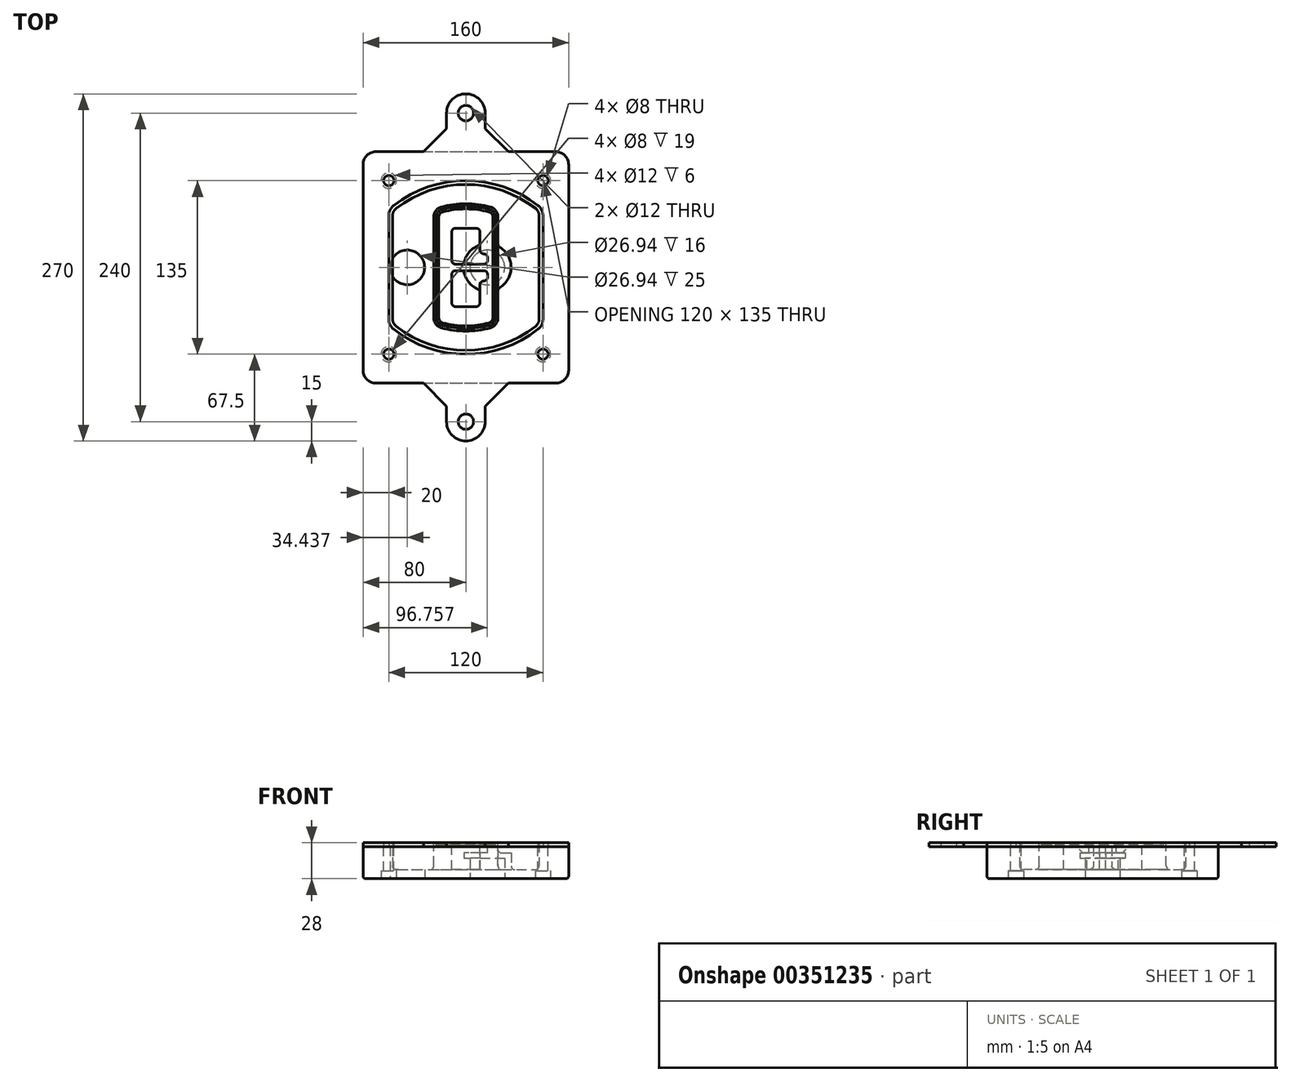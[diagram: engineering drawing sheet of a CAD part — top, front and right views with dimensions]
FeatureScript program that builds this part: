
annotation { "Feature Type Name" : "Feature", "Feature Type Description" : "" }
export const myFeature = defineFeature(function(context is Context, id is Id, definition is map)
    precondition{}
    {
        {
            var Q0;
            Q0=qCreatedBy(makeId("Top.planeOp"),FACE);
            var sketch = newSketch(context, id + "F0", { "sketchPlane" : qUnion([Q0])});
            skPoint(sketch, "E0.rect.middle", {"position": v(0, 0) * mm});
            skLineSegment(sketch, "E1.bottom", {"start": v(-70, -90) * mm, "end": v(70, -90) * mm});
            skLineSegment(sketch, "E1.top", {"start": v(-70, 90) * mm, "end": v(70, 90) * mm});
            skLineSegment(sketch, "E1.left", {"start": v(-80, -80) * mm, "end": v(-80, 80) * mm});
            skLineSegment(sketch, "E1.right", {"start": v(80, -80) * mm, "end": v(80, 80) * mm});
            skLineSegment(sketch, "E2", {"start": v(-80, 90) * mm, "end": v(80, -90) * mm, "construction": true});
            skLineSegment(sketch, "E3", {"start": v(80, 90) * mm, "end": v(-80, -90) * mm, "construction": true});
            skCircle(sketch, "E4", {"center": v(-60, 67.5) * mm, "radius": 4 * mm});
            skCircle(sketch, "E5", {"center": v(60, 67.5) * mm, "radius": 4 * mm});
            skCircle(sketch, "E6", {"center": v(60, -67.5) * mm, "radius": 4 * mm});
            skCircle(sketch, "E7", {"center": v(-60, -67.5) * mm, "radius": 4 * mm});
            skLineSegment(sketch, "E8", {"start": v(-60, 67.5) * mm, "end": v(60, 67.5) * mm, "construction": true});
            skLineSegment(sketch, "E9", {"start": v(60, 67.5) * mm, "end": v(60, -67.5) * mm, "construction": true});
            skLineSegment(sketch, "E10", {"start": v(60, -67.5) * mm, "end": v(-60, -67.5) * mm, "construction": true});
            skLineSegment(sketch, "E11", {"start": v(-60, -67.5) * mm, "end": v(-60, 67.5) * mm, "construction": true});
            skLineSegment(sketch, "E12", {"start": v(-60, 40.3) * mm, "end": v(-60, -40.3) * mm});
            skLineSegment(sketch, "E13", {"start": v(60, 40.3) * mm, "end": v(60, -40.3) * mm});
            skArc(sketch, "E14", {"start": v(56.15, 48.18) * mm, "mid": v(0, 67.5) * mm, "end": v(-56.15, 48.18) * mm});
            skArc(sketch, "E15", {"start": v(-56.15, -48.18) * mm, "mid": v(0, -67.5) * mm, "end": v(56.15, -48.18) * mm});
            skLineSegment(sketch, "E16", {"start": v(-60, 0) * mm, "end": v(60, 0) * mm, "construction": true});
            skPoint(sketch, "E17.visualSharp", {"position": v(-60, -45) * mm});
            skArc(sketch, "E17.filletArc", {"start": v(-60, -40.3) * mm, "mid": v(-58.99, -44.68) * mm, "end": v(-56.15, -48.18) * mm});
            skPoint(sketch, "E18.visualSharp", {"position": v(-60, 45) * mm});
            skArc(sketch, "E18.filletArc", {"start": v(-56.15, 48.18) * mm, "mid": v(-58.99, 44.68) * mm, "end": v(-60, 40.3) * mm});
            skPoint(sketch, "E19.visualSharp", {"position": v(60, 45) * mm});
            skArc(sketch, "E19.filletArc", {"start": v(60, 40.3) * mm, "mid": v(58.99, 44.68) * mm, "end": v(56.15, 48.18) * mm});
            skPoint(sketch, "E20.visualSharp", {"position": v(60, -45) * mm});
            skArc(sketch, "E20.filletArc", {"start": v(56.15, -48.18) * mm, "mid": v(58.99, -44.68) * mm, "end": v(60, -40.3) * mm});
            skPoint(sketch, "E21.visualSharp", {"position": v(-80, 90) * mm});
            skArc(sketch, "E21.filletArc", {"start": v(-70, 90) * mm, "mid": v(-77.07, 87.07) * mm, "end": v(-80, 80) * mm});
            skPoint(sketch, "E22.visualSharp", {"position": v(80, 90) * mm});
            skArc(sketch, "E22.filletArc", {"start": v(80, 80) * mm, "mid": v(77.07, 87.07) * mm, "end": v(70, 90) * mm});
            skPoint(sketch, "E23.visualSharp", {"position": v(80, -90) * mm});
            skArc(sketch, "E23.filletArc", {"start": v(70, -90) * mm, "mid": v(77.07, -87.07) * mm, "end": v(80, -80) * mm});
            skPoint(sketch, "E24.visualSharp", {"position": v(-80, -90) * mm});
            skArc(sketch, "E24.filletArc", {"start": v(-80, -80) * mm, "mid": v(-77.07, -87.07) * mm, "end": v(-70, -90) * mm});
            skArc(sketch, "E25.0", {"start": v(57, 40.3) * mm, "mid": v(56.3, 43.36) * mm, "end": v(54.3, 45.81) * mm});
            skLineSegment(sketch, "E25.1", {"start": v(57, 40.3) * mm, "end": v(57, -40.3) * mm});
            skArc(sketch, "E25.2", {"start": v(54.3, -45.81) * mm, "mid": v(56.3, -43.36) * mm, "end": v(57, -40.3) * mm});
            skArc(sketch, "E25.3", {"start": v(-54.3, -45.81) * mm, "mid": v(0, -64.5) * mm, "end": v(54.3, -45.81) * mm});
            skArc(sketch, "E25.4", {"start": v(-57, -40.3) * mm, "mid": v(-56.3, -43.36) * mm, "end": v(-54.3, -45.81) * mm});
            skArc(sketch, "E25.5", {"start": v(54.3, 45.81) * mm, "mid": v(0, 64.5) * mm, "end": v(-54.3, 45.81) * mm});
            skLineSegment(sketch, "E25.6", {"start": v(-57, 40.3) * mm, "end": v(-57, -40.3) * mm});
            skArc(sketch, "E25.7", {"start": v(-54.3, 45.81) * mm, "mid": v(-56.3, 43.36) * mm, "end": v(-57, 40.3) * mm});
            skArc(sketch, "E26.0", {"start": v(-58.62, 51.33) * mm, "mid": v(-62.58, 46.43) * mm, "end": v(-64, 40.3) * mm});
            skArc(sketch, "E26.1", {"start": v(58.62, 51.33) * mm, "mid": v(0, 71.5) * mm, "end": v(-58.62, 51.33) * mm});
            skArc(sketch, "E26.2", {"start": v(64, 40.3) * mm, "mid": v(62.58, 46.43) * mm, "end": v(58.62, 51.33) * mm});
            skLineSegment(sketch, "E26.3", {"start": v(64, 40.3) * mm, "end": v(64, -40.3) * mm});
            skArc(sketch, "E26.4", {"start": v(58.62, -51.33) * mm, "mid": v(62.58, -46.43) * mm, "end": v(64, -40.3) * mm});
            skLineSegment(sketch, "E26.5", {"start": v(-64, 40.3) * mm, "end": v(-64, -40.3) * mm});
            skArc(sketch, "E26.6", {"start": v(-58.62, -51.33) * mm, "mid": v(0, -71.5) * mm, "end": v(58.62, -51.33) * mm});
            skArc(sketch, "E26.7", {"start": v(-64, -40.3) * mm, "mid": v(-62.58, -46.43) * mm, "end": v(-58.62, -51.33) * mm});
            skSolve(sketch);
        }
        {
            var Q0;
            Q0=makeQuery(id+"F0.imprint","IMPRINT",FACE,{"disambiguationData":[TD([[makeQuery(id+"F0.imprint","IMPRINT",EDGE,{"derivedFrom":sQuery(id+"F0.wireOp",EDGE,"E1.bottom")}),1.0]])]});
            var Q1;
            Q1=makeQuery(id+"F0.imprint","IMPRINT",FACE,{"disambiguationData":[TD([[makeQuery(id+"F0.imprint","IMPRINT",EDGE,{"derivedFrom":sQuery(id+"F0.wireOp",EDGE,"E12")}),1.0]])]});
            var Q2;
            Q2=makeQuery(id+"F0.imprint","IMPRINT",FACE,{"disambiguationData":[TD([[makeQuery(id+"F0.imprint","IMPRINT",EDGE,{"derivedFrom":sQuery(id+"F0.wireOp",EDGE,"E25.0")}),1.0]])]});
            var Q3;
            Q3=makeQuery(id+"F0.imprint","IMPRINT",FACE,{"disambiguationData":[TD([[makeQuery(id+"F0.imprint","IMPRINT",EDGE,{"derivedFrom":sQuery(id+"F0.wireOp",EDGE,"E12")}),-1.0]])]});
            extrude(context, id + "F1", {"entities" : qUnion([Q0, Q1, Q2, Q3]), "oppositeDirection" : true, "depth" : 25 * mm});
        }
        {
            var Q0;
            Q0=makeQuery(id+"F0.imprint","IMPRINT",FACE,{"disambiguationData":[TD([[makeQuery(id+"F0.imprint","IMPRINT",EDGE,{"derivedFrom":sQuery(id+"F0.wireOp",EDGE,"E12")}),1.0]])]});
            extrude(context, id + "F2", {"entities" : qUnion([Q0]), "operationType" : NewBodyOperationType.ADD, "depth" : 3 * mm});
        }
        {
            var Q0;
            Q0=makeQuery(id+"F0.imprint","IMPRINT",FACE,{"disambiguationData":[TD([[makeQuery(id+"F0.imprint","IMPRINT",EDGE,{"derivedFrom":sQuery(id+"F0.wireOp",EDGE,"E25.0")}),1.0]])]});
            extrude(context, id + "F3", {"entities" : qUnion([Q0]), "operationType" : NewBodyOperationType.REMOVE, "oppositeDirection" : true, "depth" : 18 * mm});
        }
        {
            var Q0;
            Q0=makeQuery(id+"F2.opExtrude","CAP_FACE",FACE,{"disambiguationData":[OSD([sQuery(id+"F0.wireOp",EDGE,"E12"),sQuery(id+"F0.wireOp",EDGE,"E13"),sQuery(id+"F0.wireOp",EDGE,"E14"),sQuery(id+"F0.wireOp",EDGE,"E15"),sQuery(id+"F0.wireOp",EDGE,"E17.filletArc"),sQuery(id+"F0.wireOp",EDGE,"E18.filletArc"),sQuery(id+"F0.wireOp",EDGE,"E19.filletArc"),sQuery(id+"F0.wireOp",EDGE,"E20.filletArc"),sQuery(id+"F0.wireOp",EDGE,"E25.0"),sQuery(id+"F0.wireOp",EDGE,"E25.1"),sQuery(id+"F0.wireOp",EDGE,"E25.2"),sQuery(id+"F0.wireOp",EDGE,"E25.3"),sQuery(id+"F0.wireOp",EDGE,"E25.4"),sQuery(id+"F0.wireOp",EDGE,"E25.5"),sQuery(id+"F0.wireOp",EDGE,"E25.6"),sQuery(id+"F0.wireOp",EDGE,"E25.7")])],"isStart":false});
            var sketch = newSketch(context, id + "F4", { "sketchPlane" : qUnion([Q0])});
            skArc(sketch, "E27.0", {"start": v(-19.08, -46.97) * mm, "mid": v(0, -49.5) * mm, "end": v(19.08, -46.97) * mm});
            skArc(sketch, "E28.0", {"start": v(19.08, 46.97) * mm, "mid": v(0, 49.5) * mm, "end": v(-19.08, 46.97) * mm});
            skLineSegment(sketch, "E29", {"start": v(-25, 39.25) * mm, "end": v(-25, -39.25) * mm});
            skLineSegment(sketch, "E30", {"start": v(25, 39.25) * mm, "end": v(25, -39.25) * mm});
            skLineSegment(sketch, "E31", {"start": v(-25, 45.1) * mm, "end": v(25, 45.1) * mm, "construction": true});
            skLineSegment(sketch, "E32", {"start": v(-25, -45.1) * mm, "end": v(25, -45.1) * mm, "construction": true});
            skPoint(sketch, "E33.visualSharp", {"position": v(-25, 45.1) * mm});
            skArc(sketch, "E33.filletArc", {"start": v(-19.08, 46.97) * mm, "mid": v(-23.35, 44.11) * mm, "end": v(-25, 39.25) * mm});
            skPoint(sketch, "E34.visualSharp", {"position": v(25, 45.1) * mm});
            skArc(sketch, "E34.filletArc", {"start": v(25, 39.25) * mm, "mid": v(23.35, 44.11) * mm, "end": v(19.08, 46.97) * mm});
            skPoint(sketch, "E35.visualSharp", {"position": v(25, -45.1) * mm});
            skArc(sketch, "E35.filletArc", {"start": v(19.08, -46.97) * mm, "mid": v(23.35, -44.11) * mm, "end": v(25, -39.25) * mm});
            skPoint(sketch, "E36.visualSharp", {"position": v(-25, -45.1) * mm});
            skArc(sketch, "E36.filletArc", {"start": v(-25, -39.25) * mm, "mid": v(-23.35, -44.11) * mm, "end": v(-19.08, -46.97) * mm});
            skArc(sketch, "E37.0", {"start": v(54.3, 45.81) * mm, "mid": v(0, 64.5) * mm, "end": v(-54.3, 45.81) * mm});
            skArc(sketch, "E37.1", {"start": v(-54.3, 45.81) * mm, "mid": v(-56.3, 43.36) * mm, "end": v(-57, 40.3) * mm});
            skLineSegment(sketch, "E37.2", {"start": v(-57, 40.3) * mm, "end": v(-57, -40.3) * mm});
            skArc(sketch, "E37.3", {"start": v(-57, -40.3) * mm, "mid": v(-56.3, -43.36) * mm, "end": v(-54.3, -45.81) * mm});
            skArc(sketch, "E37.4", {"start": v(-54.3, -45.81) * mm, "mid": v(0, -64.5) * mm, "end": v(54.3, -45.81) * mm});
            skArc(sketch, "E37.5", {"start": v(54.3, -45.81) * mm, "mid": v(56.3, -43.36) * mm, "end": v(57, -40.3) * mm});
            skLineSegment(sketch, "E37.6", {"start": v(57, 40.3) * mm, "end": v(57, -40.3) * mm});
            skArc(sketch, "E37.7", {"start": v(57, 40.3) * mm, "mid": v(56.3, 43.36) * mm, "end": v(54.3, 45.81) * mm});
            skLineSegment(sketch, "E38.0", {"start": v(23, 39.25) * mm, "end": v(23, -39.25) * mm});
            skArc(sketch, "E38.1", {"start": v(18.56, -45.04) * mm, "mid": v(21.76, -42.9) * mm, "end": v(23, -39.25) * mm});
            skArc(sketch, "E38.2", {"start": v(-18.56, -45.04) * mm, "mid": v(0, -47.5) * mm, "end": v(18.56, -45.04) * mm});
            skArc(sketch, "E38.3", {"start": v(-23, -39.25) * mm, "mid": v(-21.76, -42.9) * mm, "end": v(-18.56, -45.04) * mm});
            skLineSegment(sketch, "E38.4", {"start": v(-23, 39.25) * mm, "end": v(-23, -39.25) * mm});
            skArc(sketch, "E38.5", {"start": v(23, 39.25) * mm, "mid": v(21.76, 42.9) * mm, "end": v(18.56, 45.04) * mm});
            skArc(sketch, "E38.6", {"start": v(-18.56, 45.04) * mm, "mid": v(-21.76, 42.9) * mm, "end": v(-23, 39.25) * mm});
            skArc(sketch, "E38.7", {"start": v(18.56, 45.04) * mm, "mid": v(0, 47.5) * mm, "end": v(-18.56, 45.04) * mm});
            skArc(sketch, "E39.0", {"start": v(21, 39.25) * mm, "mid": v(20.18, 41.68) * mm, "end": v(18.04, 43.1) * mm});
            skLineSegment(sketch, "E39.1", {"start": v(21, 39.25) * mm, "end": v(21, -39.25) * mm});
            skArc(sketch, "E39.2", {"start": v(18.04, -43.1) * mm, "mid": v(20.18, -41.68) * mm, "end": v(21, -39.25) * mm});
            skArc(sketch, "E39.3", {"start": v(-18.04, -43.1) * mm, "mid": v(0, -45.5) * mm, "end": v(18.04, -43.1) * mm});
            skArc(sketch, "E39.4", {"start": v(-21, -39.25) * mm, "mid": v(-20.18, -41.68) * mm, "end": v(-18.04, -43.1) * mm});
            skArc(sketch, "E39.5", {"start": v(18.04, 43.1) * mm, "mid": v(0, 45.5) * mm, "end": v(-18.04, 43.1) * mm});
            skLineSegment(sketch, "E39.6", {"start": v(-21, 39.25) * mm, "end": v(-21, -39.25) * mm});
            skArc(sketch, "E39.7", {"start": v(-18.04, 43.1) * mm, "mid": v(-20.18, 41.68) * mm, "end": v(-21, 39.25) * mm});
            skLineSegment(sketch, "E40", {"start": v(-25, 0) * mm, "end": v(25, 0) * mm, "construction": true});
            skLineSegment(sketch, "E41", {"start": v(-11, 5.5) * mm, "end": v(-11, 27.5) * mm});
            skLineSegment(sketch, "E42", {"start": v(-8, 30.5) * mm, "end": v(8, 30.5) * mm});
            skLineSegment(sketch, "E43", {"start": v(11, 27.5) * mm, "end": v(11, 13.5) * mm});
            skLineSegment(sketch, "E44", {"start": v(14, 10.5) * mm, "end": v(14, 10.5) * mm});
            skLineSegment(sketch, "E45", {"start": v(17, 7.5) * mm, "end": v(17, 5.5) * mm});
            skLineSegment(sketch, "E46", {"start": v(14, 2.5) * mm, "end": v(-8, 2.5) * mm});
            skPoint(sketch, "E47.visualSharp", {"position": v(-11, 30.5) * mm});
            skArc(sketch, "E47.filletArc", {"start": v(-8, 30.5) * mm, "mid": v(-10.12, 29.62) * mm, "end": v(-11, 27.5) * mm});
            skPoint(sketch, "E48.visualSharp", {"position": v(11, 30.5) * mm});
            skArc(sketch, "E48.filletArc", {"start": v(11, 27.5) * mm, "mid": v(10.12, 29.62) * mm, "end": v(8, 30.5) * mm});
            skPoint(sketch, "E49.visualSharp", {"position": v(11, 10.5) * mm});
            skArc(sketch, "E49.filletArc", {"start": v(11, 13.5) * mm, "mid": v(11.88, 11.38) * mm, "end": v(14, 10.5) * mm});
            skPoint(sketch, "E50.visualSharp", {"position": v(17, 10.5) * mm});
            skArc(sketch, "E50.filletArc", {"start": v(17, 7.5) * mm, "mid": v(16.12, 9.62) * mm, "end": v(14, 10.5) * mm});
            skPoint(sketch, "E51.visualSharp", {"position": v(17, 2.5) * mm});
            skArc(sketch, "E51.filletArc", {"start": v(14, 2.5) * mm, "mid": v(16.12, 3.38) * mm, "end": v(17, 5.5) * mm});
            skPoint(sketch, "E52.visualSharp", {"position": v(-11, 2.5) * mm});
            skArc(sketch, "E52.filletArc", {"start": v(-11, 5.5) * mm, "mid": v(-10.12, 3.38) * mm, "end": v(-8, 2.5) * mm});
            skLineSegment(sketch, "E53.0.MirrorCS", {"start": v(14, -2.5) * mm, "end": v(-8, -2.5) * mm});
            skArc(sketch, "E54.0.MirrorCS", {"start": v(-11, -5.5) * mm, "mid": v(-10.12, -3.38) * mm, "end": v(-8, -2.5) * mm});
            skLineSegment(sketch, "E55.0.MirrorCS", {"start": v(-11, -5.5) * mm, "end": v(-11, -27.5) * mm});
            skArc(sketch, "E56.0.MirrorCS", {"start": v(-8, -30.5) * mm, "mid": v(-10.12, -29.62) * mm, "end": v(-11, -27.5) * mm});
            skLineSegment(sketch, "E57.0.MirrorCS", {"start": v(-8, -30.5) * mm, "end": v(8, -30.5) * mm});
            skArc(sketch, "E58.0.MirrorCS", {"start": v(11, -27.5) * mm, "mid": v(10.12, -29.62) * mm, "end": v(8, -30.5) * mm});
            skLineSegment(sketch, "E59.0.MirrorCS", {"start": v(11, -27.5) * mm, "end": v(11, -13.5) * mm});
            skArc(sketch, "E60.0.MirrorCS", {"start": v(11, -13.5) * mm, "mid": v(11.88, -11.38) * mm, "end": v(14, -10.5) * mm});
            skArc(sketch, "E61.0.MirrorCS", {"start": v(17, -7.5) * mm, "mid": v(16.12, -9.62) * mm, "end": v(14, -10.5) * mm});
            skLineSegment(sketch, "E62.0.MirrorCS", {"start": v(17, -7.5) * mm, "end": v(17, -5.5) * mm});
            skArc(sketch, "E63.0.MirrorCS", {"start": v(14, -2.5) * mm, "mid": v(16.12, -3.38) * mm, "end": v(17, -5.5) * mm});
            skSolve(sketch);
        }
        {
            var Q0;
            Q0=makeQuery(id+"F4.imprint","IMPRINT",FACE,{"disambiguationData":[TD([[makeQuery(id+"F4.imprint","IMPRINT",EDGE,{"derivedFrom":sQuery(id+"F4.wireOp",EDGE,"E27.0")}),1.0]])]});
            var Q1;
            Q1=makeQuery(id+"F4.imprint","IMPRINT",FACE,{"disambiguationData":[TD([[makeQuery(id+"F4.imprint","IMPRINT",EDGE,{"derivedFrom":sQuery(id+"F4.wireOp",EDGE,"E38.0")}),-1.0]])]});
            var Q2;
            Q2=makeQuery(id+"F4.imprint","IMPRINT",FACE,{"disambiguationData":[TD([[makeQuery(id+"F4.imprint","IMPRINT",EDGE,{"derivedFrom":sQuery(id+"F4.wireOp",EDGE,"E39.0")}),1.0]])]});
            extrude(context, id + "F5", {"entities" : qUnion([Q0, Q1, Q2]), "operationType" : NewBodyOperationType.ADD, "endBound" : BoundingType.UP_TO_NEXT, "oppositeDirection" : true, "depth" : 25 * mm});
        }
        {
            var Q0;
            Q0=makeQuery(id+"F4.imprint","IMPRINT",FACE,{"disambiguationData":[TD([[makeQuery(id+"F4.imprint","IMPRINT",EDGE,{"derivedFrom":sQuery(id+"F4.wireOp",EDGE,"E38.0")}),-1.0]])]});
            extrude(context, id + "F6", {"entities" : qUnion([Q0]), "operationType" : NewBodyOperationType.REMOVE, "oppositeDirection" : true, "depth" : 2 * mm});
        }
        {
            var Q0;
            Q0=makeQuery(id+"F1.opExtrude","CAP_FACE",FACE,{"disambiguationData":[OSD([sQuery(id+"F0.wireOp",EDGE,"E1.bottom"),sQuery(id+"F0.wireOp",EDGE,"E1.top"),sQuery(id+"F0.wireOp",EDGE,"E1.left"),sQuery(id+"F0.wireOp",EDGE,"E1.right"),sQuery(id+"F0.wireOp",EDGE,"E4"),sQuery(id+"F0.wireOp",EDGE,"E5"),sQuery(id+"F0.wireOp",EDGE,"E6"),sQuery(id+"F0.wireOp",EDGE,"E7"),sQuery(id+"F0.wireOp",EDGE,"E21.filletArc"),sQuery(id+"F0.wireOp",EDGE,"E22.filletArc"),sQuery(id+"F0.wireOp",EDGE,"E23.filletArc"),sQuery(id+"F0.wireOp",EDGE,"E24.filletArc")])],"isStart":false});
            var sketch = newSketch(context, id + "F7", { "sketchPlane" : qUnion([Q0])});
            skCircle(sketch, "E64", {"center": v(16.76, 0) * mm, "radius": 13.47 * mm});
            skCircle(sketch, "E65", {"center": v(-45.56, 0) * mm, "radius": 13.47 * mm});
            skLineSegment(sketch, "E66", {"start": v(80, 0) * mm, "end": v(-80, 0) * mm});
            skCircle(sketch, "E67", {"center": v(16.76, 0) * mm, "radius": 18.47 * mm});
            skCircle(sketch, "E68", {"center": v(60, -67.5) * mm, "radius": 6 * mm});
            skCircle(sketch, "E69", {"center": v(-60, -67.5) * mm, "radius": 6 * mm});
            skCircle(sketch, "E70", {"center": v(-60, 67.5) * mm, "radius": 6 * mm});
            skCircle(sketch, "E71", {"center": v(60, 67.5) * mm, "radius": 6 * mm});
            skSolve(sketch);
        }
        {
            var Q0;
            {var subQ1=sQuery(id+"F7.wireOp",EDGE,"E66");var subQ4=sQuery(id+"F7.wireOp",EDGE,"E64");var subQ6=makeQuery(id+"F7.imprint","INTERSECT",VERTEX,{"disambiguationData":[OD(0.0)],"derivedFrom":[subQ4,subQ1]});Q0=makeQuery(id+"F7.imprint","IMPRINT",FACE,{"disambiguationData":[TD([[makeQuery(id+"F7.imprint","IMPRINT",EDGE,{"disambiguationData":[TD([[subQ6,-1.0]])],"derivedFrom":subQ4}),-1.0]])]});}
            var Q1;
            {var subQ0=sQuery(id+"F7.wireOp",EDGE,"E66");var subQ1=sQuery(id+"F7.wireOp",EDGE,"E64");var subQ3=makeQuery(id+"F7.imprint","INTERSECT",VERTEX,{"disambiguationData":[OD(0.0)],"derivedFrom":[subQ1,subQ0]});Q1=makeQuery(id+"F7.imprint","IMPRINT",FACE,{"disambiguationData":[TD([[makeQuery(id+"F7.imprint","IMPRINT",EDGE,{"disambiguationData":[TD([[subQ3,-1.0]])],"derivedFrom":subQ1}),1.0]])]});}
            var Q2;
            {var subQ0=sQuery(id+"F7.wireOp",EDGE,"E66");var subQ1=sQuery(id+"F7.wireOp",EDGE,"E64");var subQ3=makeQuery(id+"F7.imprint","INTERSECT",VERTEX,{"disambiguationData":[OD(0.0)],"derivedFrom":[subQ1,subQ0]});Q2=makeQuery(id+"F7.imprint","IMPRINT",FACE,{"disambiguationData":[TD([[makeQuery(id+"F7.imprint","IMPRINT",EDGE,{"disambiguationData":[TD([[subQ3,1.0]])],"derivedFrom":subQ1}),1.0]])]});}
            var Q3;
            {var subQ1=sQuery(id+"F7.wireOp",EDGE,"E66");var subQ4=sQuery(id+"F7.wireOp",EDGE,"E64");var subQ6=makeQuery(id+"F7.imprint","INTERSECT",VERTEX,{"disambiguationData":[OD(0.0)],"derivedFrom":[subQ4,subQ1]});Q3=makeQuery(id+"F7.imprint","IMPRINT",FACE,{"disambiguationData":[TD([[makeQuery(id+"F7.imprint","IMPRINT",EDGE,{"disambiguationData":[TD([[subQ6,1.0]])],"derivedFrom":subQ4}),-1.0]])]});}
            extrude(context, id + "F8", {"entities" : qUnion([Q0, Q1, Q2, Q3]), "operationType" : NewBodyOperationType.ADD, "oppositeDirection" : true, "depth" : 20 * mm});
        }
        {
            var Q0;
            {var subQ0=sQuery(id+"F7.wireOp",EDGE,"E66");var subQ1=sQuery(id+"F7.wireOp",EDGE,"E64");var subQ3=makeQuery(id+"F7.imprint","INTERSECT",VERTEX,{"disambiguationData":[OD(0.0)],"derivedFrom":[subQ1,subQ0]});Q0=makeQuery(id+"F7.imprint","IMPRINT",FACE,{"disambiguationData":[TD([[makeQuery(id+"F7.imprint","IMPRINT",EDGE,{"disambiguationData":[TD([[subQ3,-1.0]])],"derivedFrom":subQ1}),1.0]])]});}
            var Q1;
            {var subQ0=sQuery(id+"F7.wireOp",EDGE,"E66");var subQ1=sQuery(id+"F7.wireOp",EDGE,"E64");var subQ3=makeQuery(id+"F7.imprint","INTERSECT",VERTEX,{"disambiguationData":[OD(0.0)],"derivedFrom":[subQ1,subQ0]});Q1=makeQuery(id+"F7.imprint","IMPRINT",FACE,{"disambiguationData":[TD([[makeQuery(id+"F7.imprint","IMPRINT",EDGE,{"disambiguationData":[TD([[subQ3,1.0]])],"derivedFrom":subQ1}),1.0]])]});}
            extrude(context, id + "F9", {"entities" : qUnion([Q0, Q1]), "operationType" : NewBodyOperationType.REMOVE, "oppositeDirection" : true, "depth" : 16 * mm});
        }
        {
            var Q0;
            {var subQ0=sQuery(id+"F7.wireOp",EDGE,"E66");var subQ1=sQuery(id+"F7.wireOp",EDGE,"E65");var subQ3=makeQuery(id+"F7.imprint","INTERSECT",VERTEX,{"disambiguationData":[OD(0.0)],"derivedFrom":[subQ1,subQ0]});Q0=makeQuery(id+"F7.imprint","IMPRINT",FACE,{"disambiguationData":[TD([[makeQuery(id+"F7.imprint","IMPRINT",EDGE,{"disambiguationData":[TD([[subQ3,-1.0]])],"derivedFrom":subQ1}),1.0]])]});}
            var Q1;
            {var subQ0=sQuery(id+"F7.wireOp",EDGE,"E66");var subQ1=sQuery(id+"F7.wireOp",EDGE,"E65");var subQ3=makeQuery(id+"F7.imprint","INTERSECT",VERTEX,{"disambiguationData":[OD(0.0)],"derivedFrom":[subQ1,subQ0]});Q1=makeQuery(id+"F7.imprint","IMPRINT",FACE,{"disambiguationData":[TD([[makeQuery(id+"F7.imprint","IMPRINT",EDGE,{"disambiguationData":[TD([[subQ3,1.0]])],"derivedFrom":subQ1}),1.0]])]});}
            extrude(context, id + "F10", {"entities" : qUnion([Q0, Q1]), "operationType" : NewBodyOperationType.REMOVE, "oppositeDirection" : true, "depth" : 25 * mm});
        }
        {
            var Q0;
            Q0=makeQuery(id+"F7.imprint","IMPRINT",FACE,{"disambiguationData":[TD([[makeQuery(id+"F7.imprint","IMPRINT",EDGE,{"derivedFrom":sQuery(id+"F7.wireOp",EDGE,"E68")}),1.0]])]});
            var Q1;
            Q1=makeQuery(id+"F7.imprint","IMPRINT",FACE,{"disambiguationData":[TD([[makeQuery(id+"F7.imprint","IMPRINT",EDGE,{"derivedFrom":makeQuery(id+"F1.opExtrude","CAP_EDGE",EDGE,{"disambiguationData":[OSD([sQuery(id+"F0.wireOp",EDGE,"E5")])],"isStart":false})}),-1.0]])]});
            var Q2;
            Q2=makeQuery(id+"F7.imprint","IMPRINT",FACE,{"disambiguationData":[TD([[makeQuery(id+"F7.imprint","IMPRINT",EDGE,{"derivedFrom":sQuery(id+"F7.wireOp",EDGE,"E69")}),1.0]])]});
            var Q3;
            Q3=makeQuery(id+"F7.imprint","IMPRINT",FACE,{"disambiguationData":[TD([[makeQuery(id+"F7.imprint","IMPRINT",EDGE,{"derivedFrom":makeQuery(id+"F1.opExtrude","CAP_EDGE",EDGE,{"disambiguationData":[OSD([sQuery(id+"F0.wireOp",EDGE,"E4")])],"isStart":false})}),-1.0]])]});
            var Q4;
            Q4=makeQuery(id+"F7.imprint","IMPRINT",FACE,{"disambiguationData":[TD([[makeQuery(id+"F7.imprint","IMPRINT",EDGE,{"derivedFrom":sQuery(id+"F7.wireOp",EDGE,"E70")}),1.0]])]});
            var Q5;
            Q5=makeQuery(id+"F7.imprint","IMPRINT",FACE,{"disambiguationData":[TD([[makeQuery(id+"F7.imprint","IMPRINT",EDGE,{"derivedFrom":makeQuery(id+"F1.opExtrude","CAP_EDGE",EDGE,{"disambiguationData":[OSD([sQuery(id+"F0.wireOp",EDGE,"E7")])],"isStart":false})}),-1.0]])]});
            var Q6;
            Q6=makeQuery(id+"F7.imprint","IMPRINT",FACE,{"disambiguationData":[TD([[makeQuery(id+"F7.imprint","IMPRINT",EDGE,{"derivedFrom":sQuery(id+"F7.wireOp",EDGE,"E71")}),1.0]])]});
            var Q7;
            Q7=makeQuery(id+"F7.imprint","IMPRINT",FACE,{"disambiguationData":[TD([[makeQuery(id+"F7.imprint","IMPRINT",EDGE,{"derivedFrom":makeQuery(id+"F1.opExtrude","CAP_EDGE",EDGE,{"disambiguationData":[OSD([sQuery(id+"F0.wireOp",EDGE,"E6")])],"isStart":false})}),-1.0]])]});
            extrude(context, id + "F11", {"entities" : qUnion([Q0, Q1, Q2, Q3, Q4, Q5, Q6, Q7]), "operationType" : NewBodyOperationType.REMOVE, "oppositeDirection" : true, "depth" : 6 * mm});
        }
        {
            var Q0;
            Q0=makeQuery(id+"F9.boolean.opBoolean","COPY",FACE,{"derivedFrom":makeQuery(id+"F9.opExtrude","CAP_FACE",FACE,{"disambiguationData":[OSD([sQuery(id+"F7.wireOp",EDGE,"E64")])],"isStart":false})});
            var sketch = newSketch(context, id + "F12", { "sketchPlane" : qUnion([Q0])});
            skArc(sketch, "E72.0", {"start": v(11, 17.55) * mm, "mid": v(2.57, 11.82) * mm, "end": v(-1.54, 2.5) * mm});
            skArc(sketch, "E72.1", {"start": v(-1.54, -2.5) * mm, "mid": v(2.57, -11.82) * mm, "end": v(11, -17.55) * mm});
            skLineSegment(sketch, "E73", {"start": v(-1.54, -2.5) * mm, "end": v(14, -2.5) * mm});
            skLineSegment(sketch, "E74.0", {"start": v(14, 2.5) * mm, "end": v(-1.54, 2.5) * mm});
            skArc(sketch, "E74.1", {"start": v(14, 2.5) * mm, "mid": v(16.12, 3.38) * mm, "end": v(17, 5.5) * mm});
            skLineSegment(sketch, "E74.2", {"start": v(17, 7.5) * mm, "end": v(17, 5.5) * mm});
            skArc(sketch, "E74.3", {"start": v(17, 7.5) * mm, "mid": v(16.12, 9.62) * mm, "end": v(14, 10.5) * mm});
            skArc(sketch, "E74.4", {"start": v(11, 13.5) * mm, "mid": v(11.88, 11.38) * mm, "end": v(14, 10.5) * mm});
            skLineSegment(sketch, "E74.5", {"start": v(11, 17.55) * mm, "end": v(11, 13.5) * mm});
            skLineSegment(sketch, "E74.7", {"start": v(14, -2.5) * mm, "end": v(-1.54, -2.5) * mm});
            skArc(sketch, "E74.8", {"start": v(14, -2.5) * mm, "mid": v(16.12, -3.38) * mm, "end": v(17, -5.5) * mm});
            skLineSegment(sketch, "E74.9", {"start": v(17, -7.5) * mm, "end": v(17, -5.5) * mm});
            skArc(sketch, "E74.10", {"start": v(17, -7.5) * mm, "mid": v(16.12, -9.62) * mm, "end": v(14, -10.5) * mm});
            skArc(sketch, "E74.11", {"start": v(11, -13.5) * mm, "mid": v(11.88, -11.38) * mm, "end": v(14, -10.5) * mm});
            skLineSegment(sketch, "E74.12", {"start": v(11, -17.55) * mm, "end": v(11, -13.5) * mm});
            skPoint(sketch, "E75.orphan", {"position": v(11, -27.5) * mm});
            skPoint(sketch, "E76.orphan", {"position": v(-8, -2.5) * mm});
            skPoint(sketch, "E77.orphan", {"position": v(-8, 2.5) * mm});
            skPoint(sketch, "E78.orphan", {"position": v(11, 27.5) * mm});
            skSolve(sketch);
        }
        {
            var Q0;
            {var subQ7=sQuery(id+"F12.wireOp",EDGE,"E72.0");var subQ14=sQuery(id+"F12.wireOp",EDGE,"E72.1");var subQ16=sQuery(id+"F12.wireOp",EDGE,"E74.1");var subQ18=sQuery(id+"F12.wireOp",EDGE,"E74.8");Q0=qUnion([makeQuery(id+"F12.imprint","IMPRINT",FACE,{"disambiguationData":[TD([[makeQuery(id+"F12.imprint","IMPRINT",EDGE,{"derivedFrom":subQ7}),1.0]])]}),makeQuery(id+"F12.imprint","IMPRINT",FACE,{"disambiguationData":[TD([[makeQuery(id+"F12.imprint","IMPRINT",EDGE,{"derivedFrom":subQ14}),1.0]])]}),makeQuery(id+"F12.imprint","IMPRINT",FACE,{"disambiguationData":[TD([[makeQuery(id+"F12.imprint","IMPRINT",EDGE,{"derivedFrom":subQ16}),1.0]])]}),makeQuery(id+"F12.imprint","IMPRINT",FACE,{"disambiguationData":[TD([[makeQuery(id+"F12.imprint","IMPRINT",EDGE,{"derivedFrom":subQ18}),-1.0]])]})]);}
            var Q1;
            Q1=makeQuery(id+"F5.boolean.opBoolean","SPLIT",FACE,{"disambiguationData":[TD([makeQuery(id+"F5.opExtrude","SWEPT_FACE",FACE,{"disambiguationData":[OSD([sQuery(id+"F4.wireOp",EDGE,"E41")])]})])],"derivedFrom":makeQuery(id+"F3.boolean.opBoolean","COPY",FACE,{"derivedFrom":makeQuery(id+"F3.opExtrude","CAP_FACE",FACE,{"disambiguationData":[OSD([sQuery(id+"F0.wireOp",EDGE,"E25.0"),sQuery(id+"F0.wireOp",EDGE,"E25.1"),sQuery(id+"F0.wireOp",EDGE,"E25.2"),sQuery(id+"F0.wireOp",EDGE,"E25.3"),sQuery(id+"F0.wireOp",EDGE,"E25.4"),sQuery(id+"F0.wireOp",EDGE,"E25.5"),sQuery(id+"F0.wireOp",EDGE,"E25.6"),sQuery(id+"F0.wireOp",EDGE,"E25.7")])],"isStart":false})})});
            extrude(context, id + "F13", {"entities" : qUnion([Q0]), "operationType" : NewBodyOperationType.REMOVE, "endBound" : BoundingType.UP_TO_SURFACE, "endBoundEntityFace" : qUnion([Q1]), "depth" : 25 * mm});
        }
        {
            var Q0;
            Q0=makeQuery(id+"F3.boolean.opBoolean","COPY",EDGE,{"derivedFrom":makeQuery(id+"F3.opExtrude","CAP_EDGE",EDGE,{"disambiguationData":[OSD([sQuery(id+"F0.wireOp",EDGE,"E25.6")])],"isStart":false})});
            var Q1;
            Q1=makeQuery(id+"F8.boolean.opBoolean","INTERSECT",EDGE,{"derivedFrom":[makeQuery(id+"F5.opExtrude","SWEPT_FACE",FACE,{"disambiguationData":[OSD([sQuery(id+"F4.wireOp",EDGE,"E30")])]}),makeQuery(id+"F8.opExtrude","CAP_FACE",FACE,{"disambiguationData":[OSD([sQuery(id+"F7.wireOp",EDGE,"E67")])],"isStart":false})]});
            var Q2;
            Q2=makeQuery(id+"F8.boolean.opBoolean","INTERSECT",EDGE,{"disambiguationData":[OD(1.0)],"derivedFrom":[makeQuery(id+"F5.opExtrude","SWEPT_FACE",FACE,{"disambiguationData":[OSD([sQuery(id+"F4.wireOp",EDGE,"E30")])]}),makeQuery(id+"F8.opExtrude","SWEPT_FACE",FACE,{"disambiguationData":[OSD([sQuery(id+"F7.wireOp",EDGE,"E67")])]})]});
            var Q3;
            {var subQ0=sQuery(id+"F4.wireOp",EDGE,"E30");Q3=makeQuery(id+"F8.boolean.opBoolean","SPLIT",EDGE,{"disambiguationData":[TD([makeQuery(id+"F5.opExtrude","SWEPT_FACE",FACE,{"disambiguationData":[OSD([sQuery(id+"F4.wireOp",EDGE,"E35.filletArc")])]})])],"derivedFrom":makeQuery(id+"F5.opExtrude","CAP_EDGE",EDGE,{"disambiguationData":[OSD([subQ0])],"isStart":false})});}
            var Q4;
            {var subQ0=sQuery(id+"F0.wireOp",EDGE,"E25.7");var subQ1=sQuery(id+"F0.wireOp",EDGE,"E25.1");var subQ2=sQuery(id+"F0.wireOp",EDGE,"E25.6");var subQ3=sQuery(id+"F0.wireOp",EDGE,"E25.5");var subQ4=sQuery(id+"F0.wireOp",EDGE,"E25.4");var subQ5=sQuery(id+"F0.wireOp",EDGE,"E25.0");var subQ6=sQuery(id+"F0.wireOp",EDGE,"E25.2");var subQ7=sQuery(id+"F0.wireOp",EDGE,"E25.3");Q4=makeQuery(id+"F8.boolean.opBoolean","INTERSECT",EDGE,{"derivedFrom":[makeQuery(id+"F5.boolean.opBoolean","SPLIT",FACE,{"disambiguationData":[TD([makeQuery(id+"F2.opExtrude","SWEPT_FACE",FACE,{"disambiguationData":[OSD([subQ5])]})])],"derivedFrom":makeQuery(id+"F3.boolean.opBoolean","COPY",FACE,{"derivedFrom":makeQuery(id+"F3.opExtrude","CAP_FACE",FACE,{"disambiguationData":[OSD([subQ5,subQ1,subQ6,subQ7,subQ4,subQ3,subQ2,subQ0])],"isStart":false})})}),makeQuery(id+"F8.opExtrude","SWEPT_FACE",FACE,{"disambiguationData":[OSD([sQuery(id+"F7.wireOp",EDGE,"E67")])]})]});}
            var Q5;
            Q5=makeQuery(id+"F8.boolean.opBoolean","INTERSECT",EDGE,{"disambiguationData":[OD(0.0)],"derivedFrom":[makeQuery(id+"F5.opExtrude","SWEPT_FACE",FACE,{"disambiguationData":[OSD([sQuery(id+"F4.wireOp",EDGE,"E30")])]}),makeQuery(id+"F8.opExtrude","SWEPT_FACE",FACE,{"disambiguationData":[OSD([sQuery(id+"F7.wireOp",EDGE,"E67")])]})]});
            fillet(context, id + "F14", {"entities" : qUnion([Q0, Q1, Q2, Q3, Q4, Q5]), "radius" : 3 * mm, "tangentPropagation" : true, "allowEdgeOverflow" : false});
        }
        {
            var Q0;
            Q0=makeQuery(id+"F1.opExtrude","CAP_EDGE",EDGE,{"disambiguationData":[OSD([sQuery(id+"F0.wireOp",EDGE,"E1.bottom")])],"isStart":false});
            fillet(context, id + "F15", {"entities" : qUnion([Q0]), "radius" : 2 * mm, "tangentPropagation" : true, "allowEdgeOverflow" : false});
        }
        {
            var Q0;
            {var subQ0=sQuery(id+"F0.wireOp",EDGE,"E21.filletArc");var subQ1=sQuery(id+"F0.wireOp",EDGE,"E7");var subQ2=sQuery(id+"F0.wireOp",EDGE,"E6");var subQ3=sQuery(id+"F0.wireOp",EDGE,"E5");var subQ4=sQuery(id+"F0.wireOp",EDGE,"E4");var subQ5=sQuery(id+"F0.wireOp",EDGE,"E22.filletArc");var subQ6=sQuery(id+"F0.wireOp",EDGE,"E1.bottom");var subQ7=sQuery(id+"F0.wireOp",EDGE,"E1.right");var subQ8=sQuery(id+"F0.wireOp",EDGE,"E1.top");var subQ9=sQuery(id+"F0.wireOp",EDGE,"E1.left");var subQ10=sQuery(id+"F0.wireOp",EDGE,"E23.filletArc");var subQ11=sQuery(id+"F0.wireOp",EDGE,"E24.filletArc");Q0=makeQuery(id+"F2.boolean.opBoolean","SPLIT",FACE,{"disambiguationData":[TD([makeQuery(id+"F1.opExtrude","SWEPT_FACE",FACE,{"disambiguationData":[OSD([subQ6])]})])],"derivedFrom":makeQuery(id+"F1.opExtrude","CAP_FACE",FACE,{"disambiguationData":[OSD([subQ6,subQ8,subQ9,subQ7,subQ4,subQ3,subQ2,subQ1,subQ0,subQ5,subQ10,subQ11])],"isStart":true})});}
            var sketch = newSketch(context, id + "F16", { "sketchPlane" : qUnion([Q0])});
            skLineSegment(sketch, "E79.0", {"start": v(-70, 90) * mm, "end": v(70, 90) * mm});
            skLineSegment(sketch, "E79.1", {"start": v(80, -80) * mm, "end": v(80, 80) * mm});
            skCircle(sketch, "E79.2", {"center": v(60, -67.5) * mm, "radius": 4 * mm});
            skLineSegment(sketch, "E79.3", {"start": v(-70, -90) * mm, "end": v(70, -90) * mm});
            skCircle(sketch, "E79.4", {"center": v(-60, -67.5) * mm, "radius": 4 * mm});
            skLineSegment(sketch, "E79.5", {"start": v(-80, -80) * mm, "end": v(-80, 80) * mm});
            skCircle(sketch, "E79.6", {"center": v(-60, 67.5) * mm, "radius": 4 * mm});
            skArc(sketch, "E79.7", {"start": v(-70, 90) * mm, "mid": v(-77.07, 87.07) * mm, "end": v(-80, 80) * mm});
            skArc(sketch, "E79.8", {"start": v(80, 80) * mm, "mid": v(77.07, 87.07) * mm, "end": v(70, 90) * mm});
            skCircle(sketch, "E79.9", {"center": v(60, 67.5) * mm, "radius": 4 * mm});
            skArc(sketch, "E79.10", {"start": v(-80, -80) * mm, "mid": v(-77.07, -87.07) * mm, "end": v(-70, -90) * mm});
            skArc(sketch, "E79.11", {"start": v(70, -90) * mm, "mid": v(77.07, -87.07) * mm, "end": v(80, -80) * mm});
            skPoint(sketch, "E79.12", {"position": v(80, 0) * mm});
            skLineSegment(sketch, "E80", {"start": v(0, 90) * mm, "end": v(0, 120) * mm, "construction": true});
            skCircle(sketch, "E81", {"center": v(0, 120) * mm, "radius": 6 * mm});
            skLineSegment(sketch, "E82", {"start": v(-33, 90) * mm, "end": v(-15, 108) * mm});
            skLineSegment(sketch, "E83", {"start": v(-15, 108) * mm, "end": v(-15, 120) * mm});
            skLineSegment(sketch, "E84", {"start": v(33, 90) * mm, "end": v(15, 108) * mm});
            skLineSegment(sketch, "E85", {"start": v(15, 108) * mm, "end": v(15, 120) * mm});
            skArc(sketch, "E86", {"start": v(15, 120) * mm, "mid": v(0, 135) * mm, "end": v(-15, 120) * mm});
            skLineSegment(sketch, "E87", {"start": v(-80, 0) * mm, "end": v(80, 0) * mm, "construction": true});
            skLineSegment(sketch, "E88.MirrorCS", {"start": v(-33, -90) * mm, "end": v(-15, -108) * mm});
            skLineSegment(sketch, "E89.MirrorCS", {"start": v(-15, -108) * mm, "end": v(-15, -120) * mm});
            skArc(sketch, "E90.MirrorCS", {"start": v(15, -120) * mm, "mid": v(0, -135) * mm, "end": v(-15, -120) * mm});
            skLineSegment(sketch, "E91.MirrorCS", {"start": v(15, -108) * mm, "end": v(15, -120) * mm});
            skLineSegment(sketch, "E92.MirrorCS", {"start": v(33, -90) * mm, "end": v(15, -108) * mm});
            skCircle(sketch, "E93.MirrorC", {"center": v(0, -120) * mm, "radius": 6 * mm});
            skLineSegment(sketch, "E94.MirrorCS", {"start": v(0, -90) * mm, "end": v(0, -120) * mm, "construction": true});
            skSolve(sketch);
        }
        {
            var Q0;
            Q0=makeQuery(id+"F16.imprint","IMPRINT",FACE,{"disambiguationData":[TD([[makeQuery(id+"F16.imprint","IMPRINT",EDGE,{"derivedFrom":sQuery(id+"F16.wireOp",EDGE,"E81")}),-1.0]])]});
            var Q1;
            Q1=makeQuery(id+"F16.imprint","IMPRINT",FACE,{"disambiguationData":[TD([[makeQuery(id+"F16.imprint","IMPRINT",EDGE,{"derivedFrom":sQuery(id+"F16.wireOp",EDGE,"E79.1")}),1.0]])]});
            var Q2;
            {var subQ0=sQuery(id+"F16.wireOp",EDGE,"E88.MirrorCS");Q2=makeQuery(id+"F16.imprint","IMPRINT",FACE,{"disambiguationData":[TD([[makeQuery(id+"F16.imprint","IMPRINT",EDGE,{"derivedFrom":subQ0}),1.0]])]});}
            var Q3;
            Q3=makeQuery(id+"F2.opExtrude","CAP_FACE",FACE,{"disambiguationData":[OSD([sQuery(id+"F0.wireOp",EDGE,"E12"),sQuery(id+"F0.wireOp",EDGE,"E13"),sQuery(id+"F0.wireOp",EDGE,"E14"),sQuery(id+"F0.wireOp",EDGE,"E15"),sQuery(id+"F0.wireOp",EDGE,"E17.filletArc"),sQuery(id+"F0.wireOp",EDGE,"E18.filletArc"),sQuery(id+"F0.wireOp",EDGE,"E19.filletArc"),sQuery(id+"F0.wireOp",EDGE,"E20.filletArc"),sQuery(id+"F0.wireOp",EDGE,"E25.0"),sQuery(id+"F0.wireOp",EDGE,"E25.1"),sQuery(id+"F0.wireOp",EDGE,"E25.2"),sQuery(id+"F0.wireOp",EDGE,"E25.3"),sQuery(id+"F0.wireOp",EDGE,"E25.4"),sQuery(id+"F0.wireOp",EDGE,"E25.5"),sQuery(id+"F0.wireOp",EDGE,"E25.6"),sQuery(id+"F0.wireOp",EDGE,"E25.7")])],"isStart":false});
            extrude(context, id + "F17", {"entities" : qUnion([Q0, Q1, Q2]), "endBound" : BoundingType.UP_TO_SURFACE, "endBoundEntityFace" : qUnion([Q3]), "depth" : 25 * mm});
        }
    });
